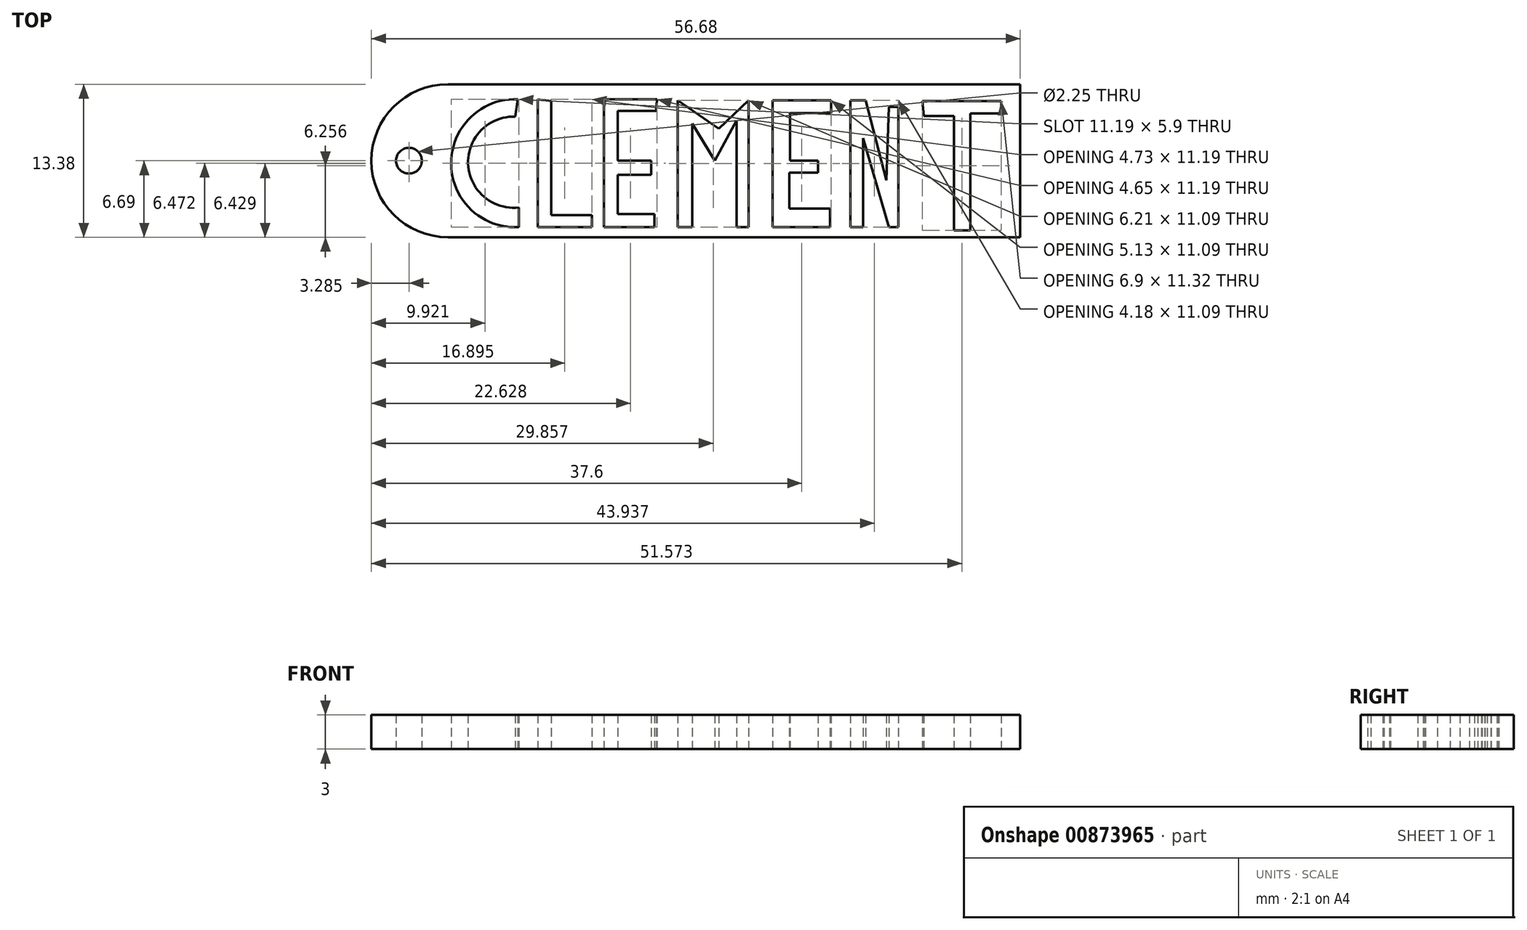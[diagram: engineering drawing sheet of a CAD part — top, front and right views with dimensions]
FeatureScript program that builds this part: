
annotation { "Feature Type Name" : "Feature", "Feature Type Description" : "" }
export const myFeature = defineFeature(function(context is Context, id is Id, definition is map)
    precondition{}
    {
        {
            var Q0;
            Q0=qCreatedBy(makeId("Top.planeOp"),FACE);
            var sketch = newSketch(context, id + "F0", { "sketchPlane" : qUnion([Q0])});
            skLineSegment(sketch, "E0.bottom", {"start": v(14.18, 6.69) * mm, "end": v(-14.18, 6.69) * mm});
            skLineSegment(sketch, "E0.top", {"start": v(14.18, -6.69) * mm, "end": v(-14.18, -6.69) * mm});
            skLineSegment(sketch, "E0.right", {"start": v(-14.18, 6.69) * mm, "end": v(-14.18, -6.69) * mm});
            skPoint(sketch, "E0.middle", {"position": v(0, 0) * mm});
            skArc(sketch, "E1", {"start": v(-14.18, 6.69) * mm, "mid": v(-20.86, 0) * mm, "end": v(-14.18, -6.69) * mm});
            skArc(sketch, "E2", {"start": v(-8.06, 5.37) * mm, "mid": v(-13.9, -0.25) * mm, "end": v(-7.99, -5.81) * mm});
            skArc(sketch, "E3", {"start": v(-8.3, 3.86) * mm, "mid": v(-12.4, -0.28) * mm, "end": v(-7.99, -4.08) * mm});
            skLineSegment(sketch, "E4", {"start": v(-7.99, -5.81) * mm, "end": v(-7.99, -4.08) * mm});
            skLineSegment(sketch, "E5", {"start": v(-8.06, 5.37) * mm, "end": v(-8.3, 3.86) * mm});
            skLineSegment(sketch, "E6", {"start": v(-6.33, 5.37) * mm, "end": v(-6.33, -5.81) * mm});
            skLineSegment(sketch, "E7", {"start": v(-6.33, -5.81) * mm, "end": v(-1.6, -5.81) * mm});
            skLineSegment(sketch, "E8", {"start": v(-1.6, -5.81) * mm, "end": v(-1.6, -4.76) * mm});
            skLineSegment(sketch, "E9", {"start": v(-1.6, -4.76) * mm, "end": v(-5.14, -4.76) * mm});
            skLineSegment(sketch, "E10", {"start": v(-5.14, -4.76) * mm, "end": v(-5.14, 5.23) * mm});
            skLineSegment(sketch, "E11", {"start": v(-5.14, 5.23) * mm, "end": v(-6.33, 5.37) * mm});
            skLineSegment(sketch, "E12", {"start": v(-0.55, 5.37) * mm, "end": v(-0.55, -5.81) * mm});
            skLineSegment(sketch, "E13", {"start": v(-0.55, -5.81) * mm, "end": v(3.86, -5.81) * mm});
            skLineSegment(sketch, "E14", {"start": v(3.86, -5.81) * mm, "end": v(3.86, -4.64) * mm});
            skLineSegment(sketch, "E15", {"start": v(3.86, -4.64) * mm, "end": v(0.66, -4.64) * mm});
            skLineSegment(sketch, "E16", {"start": v(0.66, -4.64) * mm, "end": v(0.66, -1.22) * mm});
            skLineSegment(sketch, "E17", {"start": v(0.66, 0) * mm, "end": v(0.66, 4.35) * mm});
            skLineSegment(sketch, "E18", {"start": v(0.66, 0) * mm, "end": v(3.57, 0) * mm});
            skLineSegment(sketch, "E19", {"start": v(3.57, 0) * mm, "end": v(3.57, -1.22) * mm});
            skLineSegment(sketch, "E20", {"start": v(0.66, -1.22) * mm, "end": v(3.57, -1.22) * mm});
            skLineSegment(sketch, "E21", {"start": v(0.66, 4.35) * mm, "end": v(4.03, 4.35) * mm});
            skLineSegment(sketch, "E22", {"start": v(-0.55, 5.37) * mm, "end": v(4.1, 5.37) * mm});
            skLineSegment(sketch, "E23", {"start": v(4.1, 5.37) * mm, "end": v(4.03, 4.35) * mm});
            skLineSegment(sketch, "E24", {"start": v(5.9, 5.28) * mm, "end": v(5.9, -5.8) * mm});
            skLineSegment(sketch, "E25", {"start": v(5.9, -5.8) * mm, "end": v(7.17, -5.8) * mm});
            skLineSegment(sketch, "E26", {"start": v(7.17, -5.8) * mm, "end": v(7.17, 3.25) * mm});
            skLineSegment(sketch, "E27", {"start": v(7.17, 3.25) * mm, "end": v(9.14, 0) * mm});
            skLineSegment(sketch, "E28", {"start": v(9.14, 0) * mm, "end": v(11.06, 3.54) * mm});
            skLineSegment(sketch, "E29", {"start": v(11.06, 3.54) * mm, "end": v(11.06, -5.8) * mm});
            skLineSegment(sketch, "E30", {"start": v(11.06, -5.8) * mm, "end": v(12.1, -5.8) * mm});
            skLineSegment(sketch, "E31", {"start": v(12.1, -5.8) * mm, "end": v(12.1, 5.28) * mm});
            skLineSegment(sketch, "E32", {"start": v(12.1, 5.28) * mm, "end": v(9.5, 2.79) * mm});
            skLineSegment(sketch, "E33", {"start": v(9.5, 2.79) * mm, "end": v(5.9, 5.28) * mm});
            skLineSegment(sketch, "E34", {"start": v(14.18, 5.28) * mm, "end": v(14.18, -5.8) * mm});
            skLineSegment(sketch, "E35", {"start": v(14.18, -5.8) * mm, "end": v(19.19, -5.8) * mm});
            skLineSegment(sketch, "E36", {"start": v(19.19, -5.8) * mm, "end": v(19.19, -4.18) * mm});
            skLineSegment(sketch, "E37", {"start": v(19.19, -4.18) * mm, "end": v(15.64, -4.18) * mm});
            skLineSegment(sketch, "E38", {"start": v(15.64, -4.18) * mm, "end": v(15.64, -1.05) * mm});
            skLineSegment(sketch, "E39", {"start": v(15.64, -1.05) * mm, "end": v(18.14, -1.05) * mm});
            skLineSegment(sketch, "E40", {"start": v(18.14, -1.05) * mm, "end": v(18.14, 0) * mm});
            skLineSegment(sketch, "E41", {"start": v(18.14, 0) * mm, "end": v(15.7, 0) * mm});
            skLineSegment(sketch, "E42", {"start": v(15.7, 0) * mm, "end": v(15.7, 4.18) * mm});
            skLineSegment(sketch, "E43", {"start": v(15.7, 4.18) * mm, "end": v(19.3, 4.18) * mm});
            skLineSegment(sketch, "E44", {"start": v(19.3, 4.18) * mm, "end": v(19.3, 5.28) * mm});
            skLineSegment(sketch, "E45", {"start": v(19.3, 5.28) * mm, "end": v(14.18, 5.28) * mm});
            skLineSegment(sketch, "E46", {"start": v(20.99, -5.8) * mm, "end": v(20.99, 5.28) * mm});
            skLineSegment(sketch, "E47", {"start": v(20.99, 5.28) * mm, "end": v(22.32, 5.28) * mm});
            skLineSegment(sketch, "E48", {"start": v(22.32, 5.28) * mm, "end": v(25.17, -5.8) * mm});
            skLineSegment(sketch, "E49", {"start": v(20.99, -5.8) * mm, "end": v(22.09, -5.8) * mm});
            skLineSegment(sketch, "E50", {"start": v(22.09, -5.8) * mm, "end": v(22.09, 1.97) * mm});
            skLineSegment(sketch, "E51", {"start": v(22.09, 1.97) * mm, "end": v(24.35, -5.8) * mm});
            skLineSegment(sketch, "E52", {"start": v(24.35, -5.8) * mm, "end": v(25.17, -5.8) * mm});
            skLineSegment(sketch, "E53", {"start": v(24.11, -1.7) * mm, "end": v(24.35, 4.7) * mm});
            skLineSegment(sketch, "E54", {"start": v(24.35, 4.7) * mm, "end": v(25.17, 4.67) * mm});
            skLineSegment(sketch, "E55", {"start": v(25.17, 4.67) * mm, "end": v(25.17, -5.8) * mm});
            skLineSegment(sketch, "E56", {"start": v(27.26, 5.23) * mm, "end": v(34.17, 5.23) * mm});
            skLineSegment(sketch, "E57", {"start": v(34.17, 5.23) * mm, "end": v(34.17, 4.13) * mm});
            skLineSegment(sketch, "E58", {"start": v(34.17, 4.13) * mm, "end": v(31.47, 4.13) * mm});
            skLineSegment(sketch, "E59", {"start": v(31.47, 4.13) * mm, "end": v(31.47, -6.1) * mm});
            skLineSegment(sketch, "E60", {"start": v(31.47, -6.1) * mm, "end": v(30.02, -6.1) * mm});
            skLineSegment(sketch, "E61", {"start": v(30.02, -6.1) * mm, "end": v(30.02, 3.92) * mm});
            skLineSegment(sketch, "E62", {"start": v(30.02, 3.92) * mm, "end": v(27.4, 3.92) * mm});
            skLineSegment(sketch, "E63", {"start": v(27.4, 3.92) * mm, "end": v(27.26, 5.23) * mm});
            skLineSegment(sketch, "E64", {"start": v(14.18, 6.69) * mm, "end": v(35.82, 6.69) * mm});
            skLineSegment(sketch, "E65", {"start": v(14.18, -6.69) * mm, "end": v(35.82, -6.69) * mm});
            skLineSegment(sketch, "E66", {"start": v(35.82, -6.69) * mm, "end": v(35.82, 6.69) * mm});
            skCircle(sketch, "E67", {"center": v(-17.57, 0) * mm, "radius": 1.13 * mm});
            skSolve(sketch);
        }
        {
            var Q0;
            Q0 = qSketchRegion(id + "F0", true);
            extrude(context, id + "F1", {"entities" : qUnion([Q0]), "depth" : 3 * mm, "offsetDistance" : 25.4 * mm});
        }
    });
